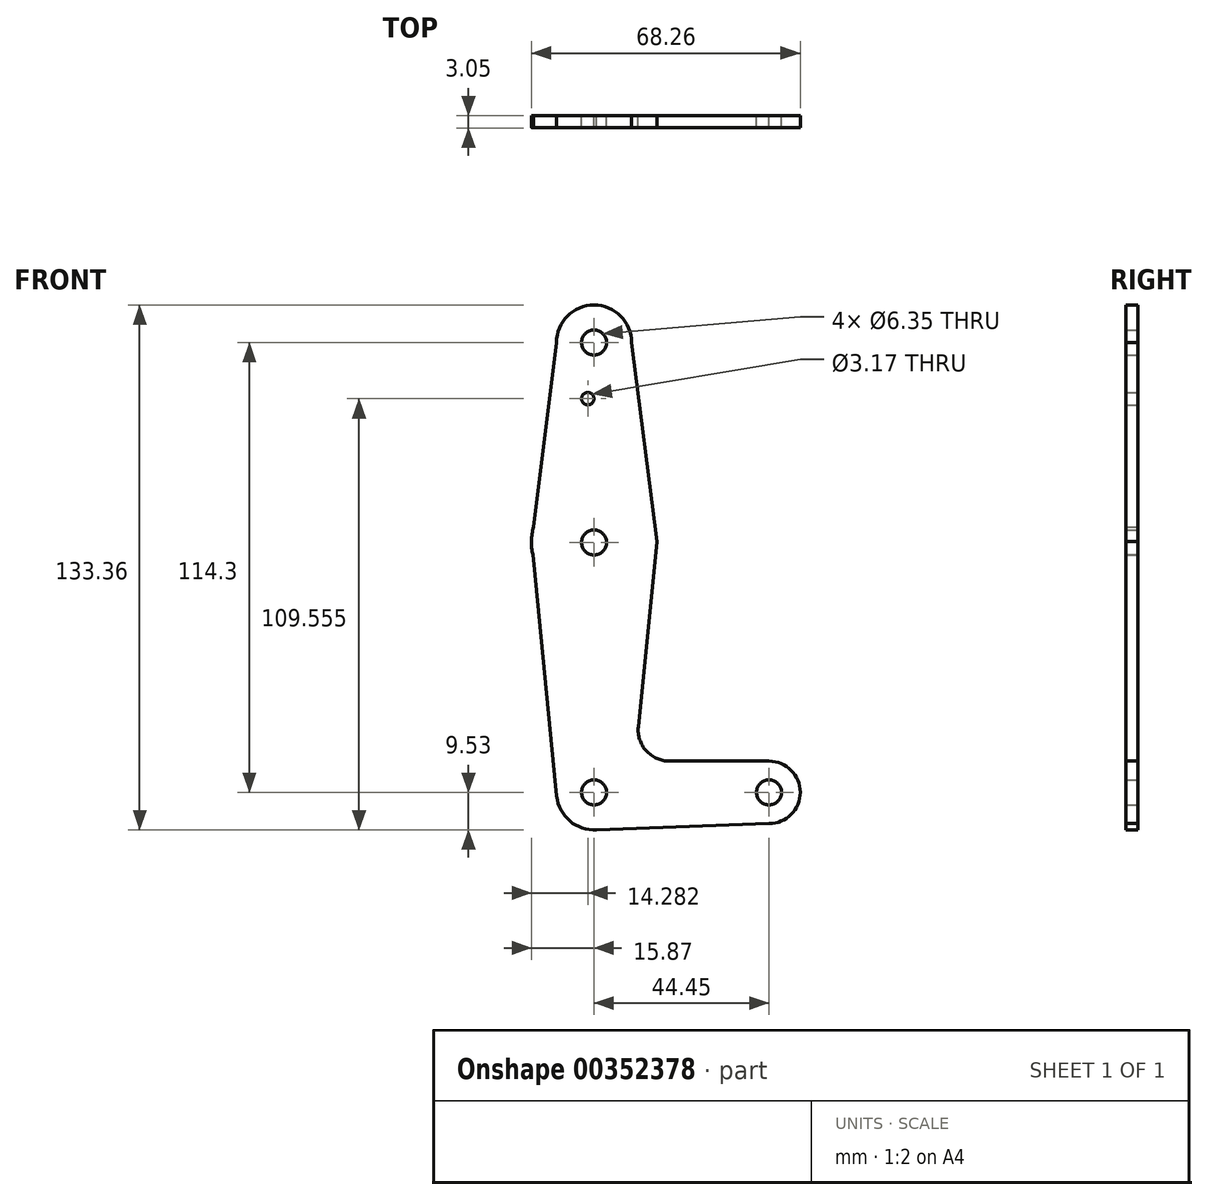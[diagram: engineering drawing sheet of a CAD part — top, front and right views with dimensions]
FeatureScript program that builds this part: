
annotation { "Feature Type Name" : "Feature", "Feature Type Description" : "" }
export const myFeature = defineFeature(function(context is Context, id is Id, definition is map)
    precondition{}
    {
        {
            var Q0;
            Q0=qCreatedBy(makeId("Front.planeOp"),FACE);
            var sketch = newSketch(context, id + "F0", { "sketchPlane" : qUnion([Q0])});
            skLineSegment(sketch, "E0", {"start": v(0, 0) * mm, "end": v(44.45, 0) * mm, "construction": true});
            skLineSegment(sketch, "E1", {"start": v(0, 0) * mm, "end": v(0, 114.3) * mm, "construction": true});
            skCircle(sketch, "E2", {"center": v(0, 0) * mm, "radius": 9.53 * mm});
            skCircle(sketch, "E3", {"center": v(44.45, 0) * mm, "radius": 7.94 * mm});
            skCircle(sketch, "E4", {"center": v(0, 114.3) * mm, "radius": 9.53 * mm});
            skCircle(sketch, "E5", {"center": v(0, 63.5) * mm, "radius": 15.88 * mm});
            skLineSegment(sketch, "E6", {"start": v(9.53, 114.3) * mm, "end": v(15.98, 63.71) * mm});
            skLineSegment(sketch, "E7", {"start": v(15.98, 63.71) * mm, "end": v(11.25, 16.68) * mm});
            skLineSegment(sketch, "E8", {"start": v(-9.52, 114.3) * mm, "end": v(-15.88, 63.5) * mm});
            skLineSegment(sketch, "E9", {"start": v(19.16, 7.94) * mm, "end": v(44.45, 7.94) * mm});
            skLineSegment(sketch, "E10", {"start": v(0, -9.52) * mm, "end": v(44.45, -7.94) * mm});
            skCircle(sketch, "E11", {"center": v(0, 114.3) * mm, "radius": 3.18 * mm});
            skCircle(sketch, "E12", {"center": v(0, 63.5) * mm, "radius": 3.18 * mm});
            skCircle(sketch, "E13", {"center": v(0, 0) * mm, "radius": 3.18 * mm});
            skCircle(sketch, "E14", {"center": v(44.45, 0) * mm, "radius": 3.18 * mm});
            skCircle(sketch, "E15", {"center": v(-1.59, 100.03) * mm, "radius": 1.59 * mm});
            skArc(sketch, "E16.filletArc", {"start": v(11.25, 16.68) * mm, "mid": v(13.26, 10.55) * mm, "end": v(19.16, 7.94) * mm});
            skLineSegment(sketch, "E17", {"start": v(-15.88, 63.5) * mm, "end": v(-9.48, -0.94) * mm});
            skSolve(sketch);
        }
        {
            var Q0;
            Q0=qSketchRegion(id+"F0",true);
            extrude(context, id + "F1", {"entities" : qUnion([Q0]), "depth" : 3.05 * mm});
        }
    });
